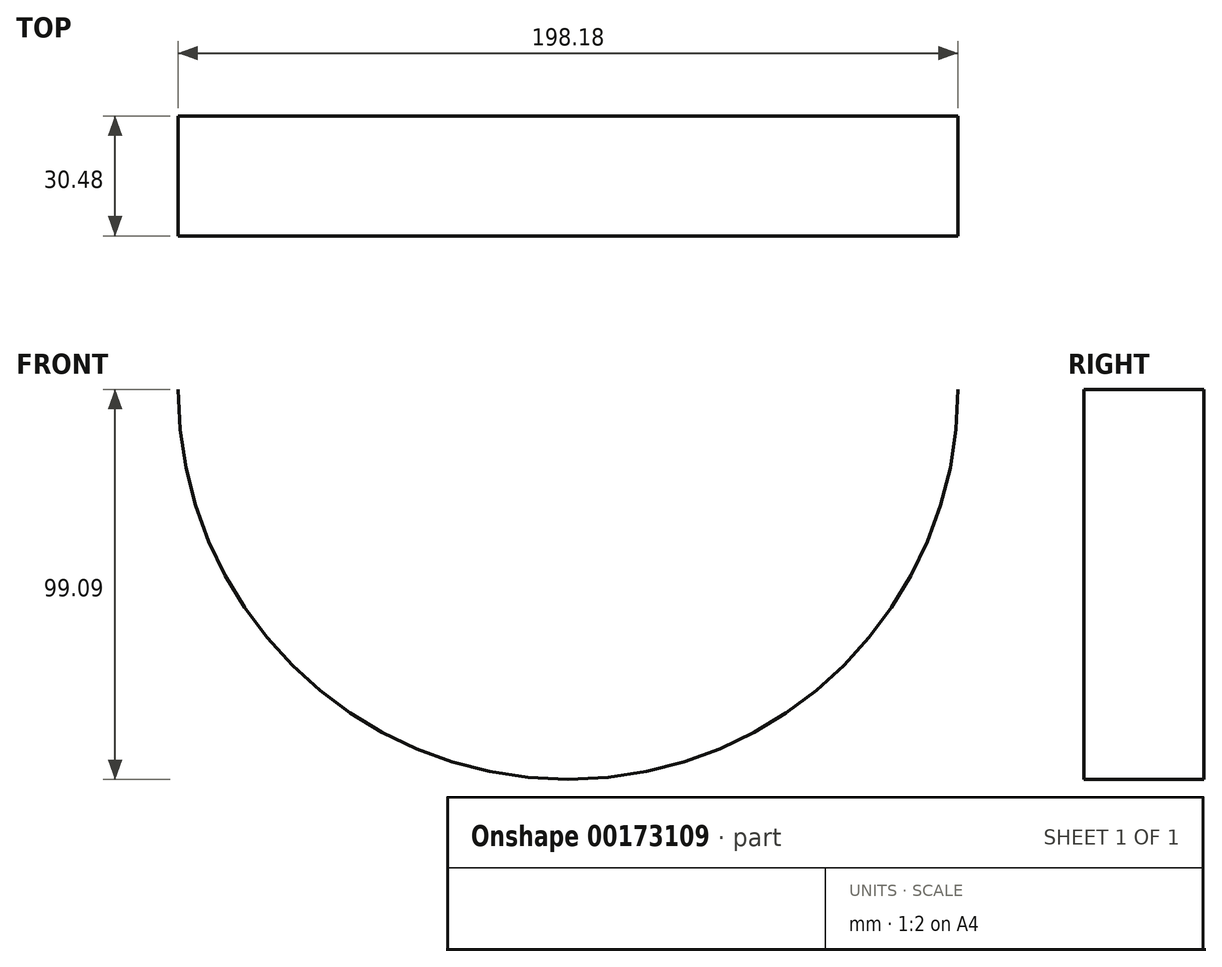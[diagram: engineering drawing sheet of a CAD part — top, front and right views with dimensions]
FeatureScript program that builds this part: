
annotation { "Feature Type Name" : "Feature", "Feature Type Description" : "" }
export const myFeature = defineFeature(function(context is Context, id is Id, definition is map)
    precondition{}
    {
        {
            var Q0;
            Q0=qCreatedBy(makeId("Front.planeOp"),FACE);
            var sketch = newSketch(context, id + "F0", { "sketchPlane" : qUnion([Q0])});
            skArc(sketch, "E0", {"start": v(-99.1, 0) * mm, "mid": v(0, -99.1) * mm, "end": v(99.1, 0) * mm});
            skSolve(sketch);
        }
        {
            var Q0;
            Q0=sQuery(id+"F0.wireOp",EDGE,"E0");
            extrude(context, id + "F2", {"bodyType" : ToolBodyType.SURFACE, "surfaceEntities" : qUnion([Q0]), "depth" : 30.48 * mm});
        }
    });
